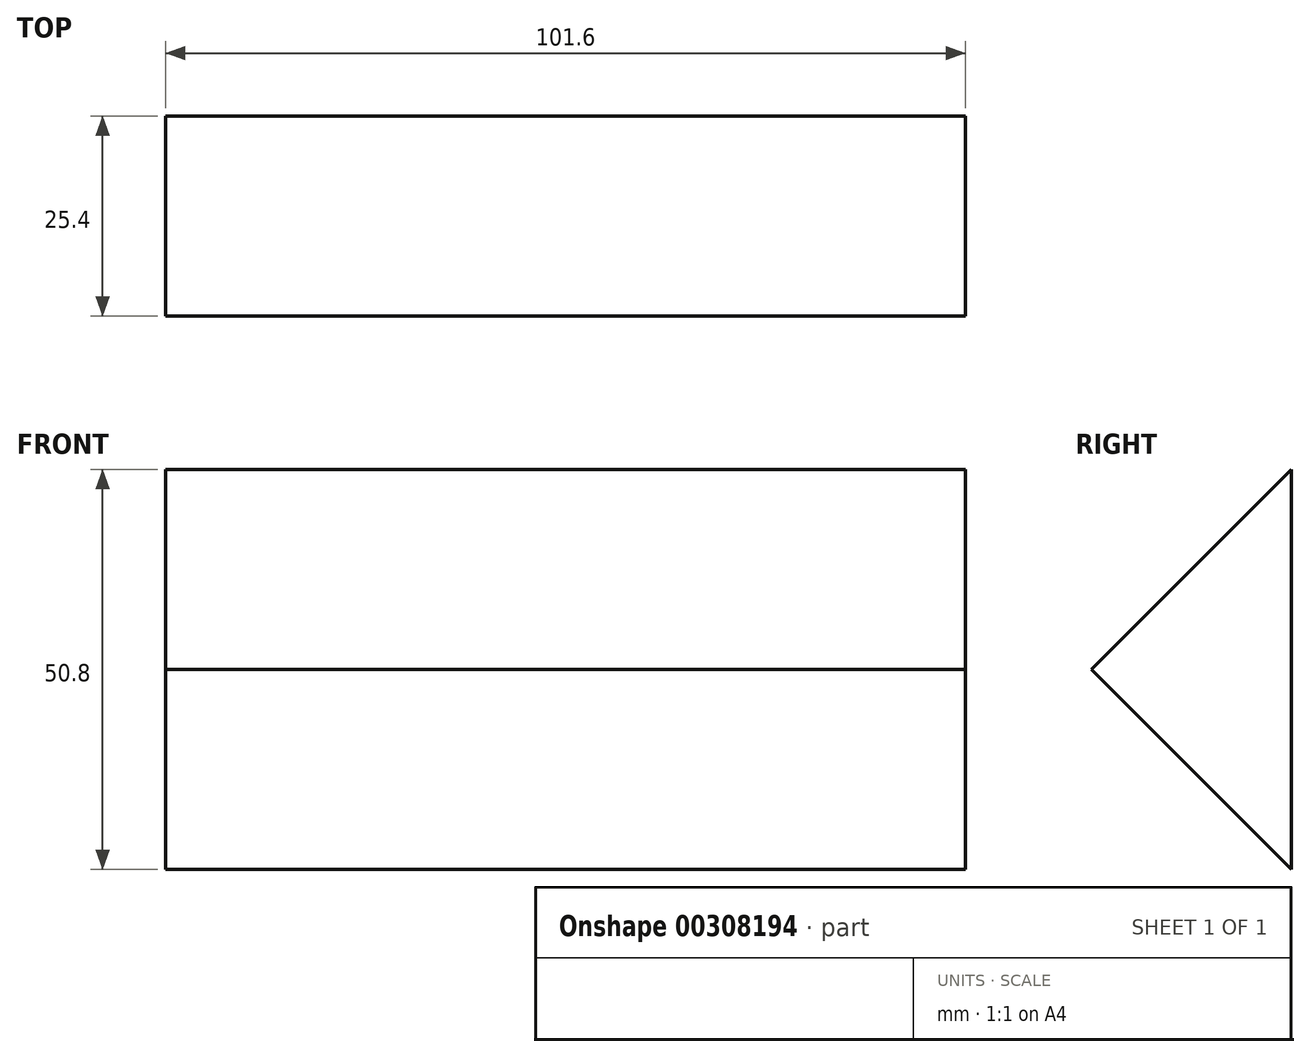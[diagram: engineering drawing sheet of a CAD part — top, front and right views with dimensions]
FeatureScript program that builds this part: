
annotation { "Feature Type Name" : "Feature", "Feature Type Description" : "" }
export const myFeature = defineFeature(function(context is Context, id is Id, definition is map)
    precondition{}
    {
        {
            var Q0;
            Q0=qCreatedBy(makeId("Front.planeOp"),FACE);
            var sketch = newSketch(context, id + "F0", { "sketchPlane" : qUnion([Q0])});
            skLineSegment(sketch, "E0.bottom", {"start": v(50.8, -25.4) * mm, "end": v(-50.8, -25.4) * mm});
            skLineSegment(sketch, "E0.top", {"start": v(50.8, 25.4) * mm, "end": v(-50.8, 25.4) * mm});
            skLineSegment(sketch, "E0.left", {"start": v(50.8, -25.4) * mm, "end": v(50.8, 25.4) * mm});
            skLineSegment(sketch, "E0.right", {"start": v(-50.8, -25.4) * mm, "end": v(-50.8, 25.4) * mm});
            skPoint(sketch, "E0.middle", {"position": v(0, 0) * mm});
            skSolve(sketch);
        }
        {
            var Q0;
            Q0 = qSketchRegion(id + "F0", true);
            extrude(context, id + "F1", {"entities" : qUnion([Q0]), "depth" : 25.4 * mm});
        }
        {
            var Q0;
            Q0=makeQuery(id+"F1.opExtrude","SWEPT_FACE",FACE,{"disambiguationData":[OSD([sQuery(id+"F0.wireOp",EDGE,"E0.left")])]});
            var sketch = newSketch(context, id + "F2", { "sketchPlane" : qUnion([Q0])});
            skPoint(sketch, "E1", {"position": v(-25.4, 0) * mm});
            skLineSegment(sketch, "E2", {"start": v(-25.4, 0) * mm, "end": v(0, -25.4) * mm});
            skLineSegment(sketch, "E3", {"start": v(-25.4, 0) * mm, "end": v(0, 25.4) * mm});
            skSolve(sketch);
        }
        {
            var Q0;
            Q0=makeQuery(id+"F1.opExtrude","SWEPT_FACE",FACE,{"disambiguationData":[OSD([sQuery(id+"F0.wireOp",EDGE,"E0.right")])]});
            var sketch = newSketch(context, id + "F3", { "sketchPlane" : qUnion([Q0])});
            skLineSegment(sketch, "E4", {"start": v(25.4, 0) * mm, "end": v(0, -25.4) * mm});
            skLineSegment(sketch, "E5", {"start": v(25.4, 0) * mm, "end": v(0, 25.4) * mm});
            skSolve(sketch);
        }
        {
            var Q0;
            {var subQ0=sQuery(id+"F2.wireOp",EDGE,"E3");Q0=makeQuery(id+"F2.imprint","IMPRINT",FACE,{"disambiguationData":[TD([[makeQuery(id+"F2.imprint","IMPRINT",EDGE,{"derivedFrom":subQ0}),1.0]])]});}
            extrude(context, id + "F4", {"entities" : qUnion([Q0]), "operationType" : NewBodyOperationType.REMOVE, "oppositeDirection" : true, "depth" : 101.6 * mm});
        }
        {
            var Q0;
            {var subQ0=sQuery(id+"F3.wireOp",EDGE,"E4");Q0=makeQuery(id+"F3.imprint","IMPRINT",FACE,{"disambiguationData":[TD([[makeQuery(id+"F3.imprint","IMPRINT",EDGE,{"derivedFrom":subQ0}),1.0]])]});}
            extrude(context, id + "F5", {"entities" : qUnion([Q0]), "operationType" : NewBodyOperationType.REMOVE, "oppositeDirection" : true, "depth" : 101.6 * mm});
        }
    });
